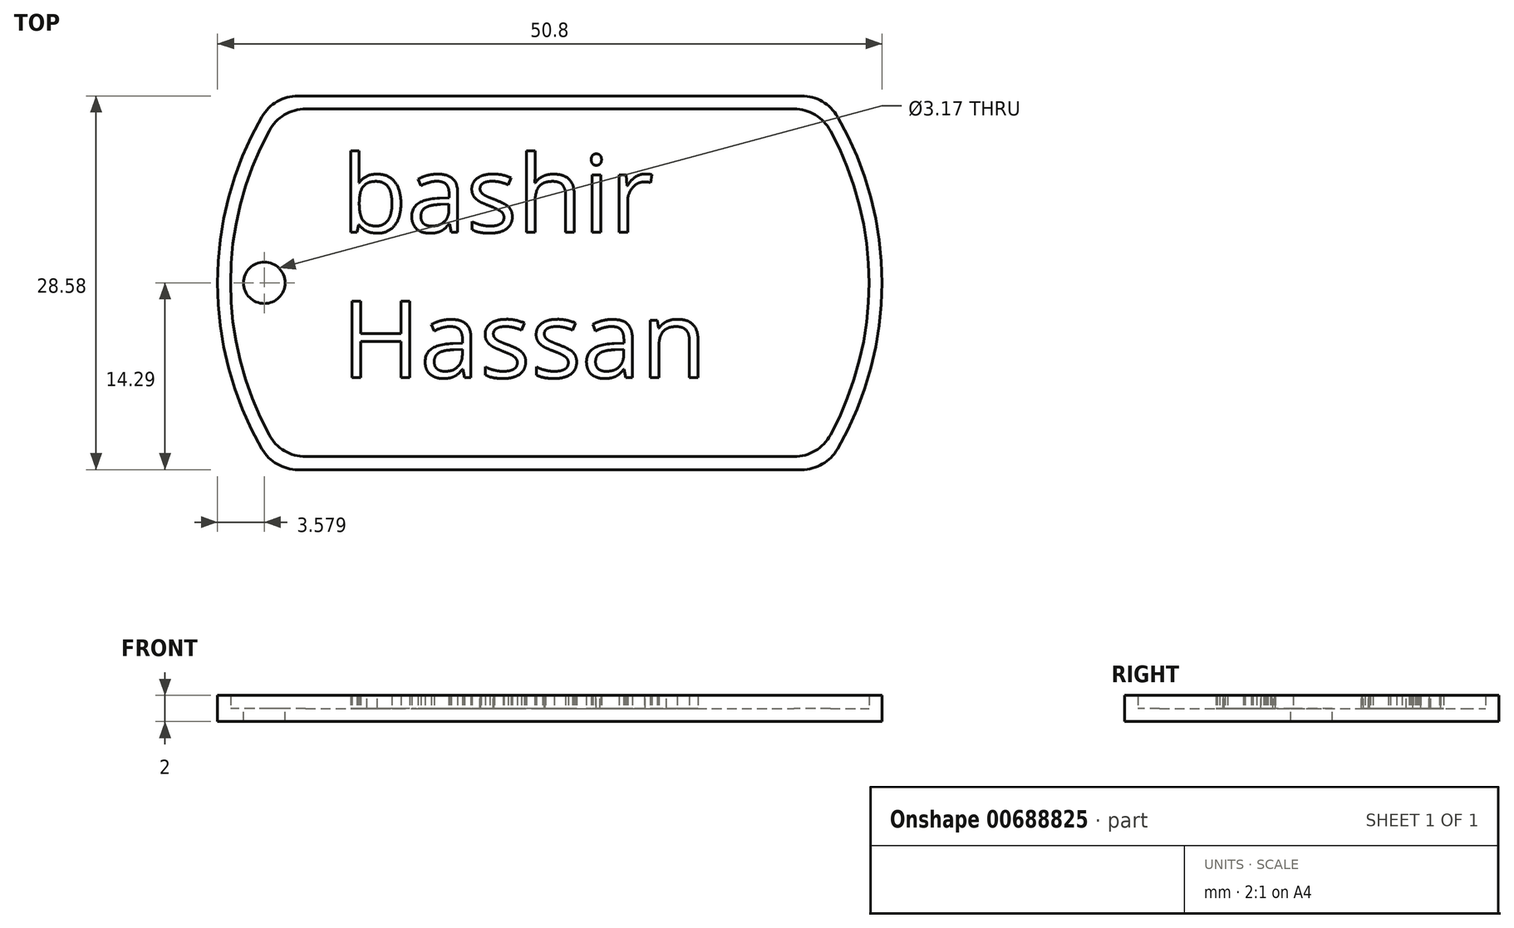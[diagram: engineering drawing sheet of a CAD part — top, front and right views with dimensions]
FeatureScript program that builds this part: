
annotation { "Feature Type Name" : "Feature", "Feature Type Description" : "" }
export const myFeature = defineFeature(function(context is Context, id is Id, definition is map)
    precondition{}
    {
        {
            var Q0;
            Q0=qCreatedBy(makeId("Top.planeOp"),FACE);
            var sketch = newSketch(context, id + "F0", { "sketchPlane" : qUnion([Q0])});
            skArc(sketch, "E0", {"start": v(-22, 12.7) * mm, "mid": v(-25.4, 0) * mm, "end": v(-22, -12.7) * mm});
            skLineSegment(sketch, "E1.top", {"start": v(-19.25, -14.29) * mm, "end": v(19.25, -14.29) * mm});
            skArc(sketch, "E2.trimOffspring", {"start": v(22, -12.7) * mm, "mid": v(25.4, 0) * mm, "end": v(22, 12.7) * mm});
            skLineSegment(sketch, "E3", {"start": v(-19.25, 14.29) * mm, "end": v(19.25, 14.29) * mm});
            skPoint(sketch, "E4.visualSharp", {"position": v(-21, 14.29) * mm});
            skArc(sketch, "E4.filletArc", {"start": v(-19.25, 14.29) * mm, "mid": v(-20.83, 13.86) * mm, "end": v(-22, 12.7) * mm});
            skPoint(sketch, "E5.visualSharp", {"position": v(21, 14.29) * mm});
            skArc(sketch, "E5.filletArc", {"start": v(22, 12.7) * mm, "mid": v(20.83, 13.86) * mm, "end": v(19.25, 14.29) * mm});
            skPoint(sketch, "E6.visualSharp", {"position": v(21, -14.29) * mm});
            skArc(sketch, "E6.filletArc", {"start": v(19.25, -14.29) * mm, "mid": v(20.83, -13.86) * mm, "end": v(22, -12.7) * mm});
            skPoint(sketch, "E7.visualSharp", {"position": v(-21, -14.29) * mm});
            skArc(sketch, "E7.filletArc", {"start": v(-22, -12.7) * mm, "mid": v(-20.83, -13.86) * mm, "end": v(-19.25, -14.29) * mm});
            skSolve(sketch);
        }
        {
            var Q0;
            Q0=makeQuery(id+"F0.imprint","IMPRINT",FACE,{"disambiguationData":[TD([[makeQuery(id+"F0.imprint","IMPRINT",EDGE,{"derivedFrom":sQuery(id+"F0.wireOp",EDGE,"E0")}),1.0]])]});
            extrude(context, id + "F1", {"entities" : qUnion([Q0]), "depth" : 1 * mm, "offsetDistance" : 25.4 * mm});
        }
        {
            var Q0;
            Q0=makeQuery(id+"F1.opExtrude","CAP_FACE",FACE,{"disambiguationData":[OSD([sQuery(id+"F0.wireOp",EDGE,"E0"),sQuery(id+"F0.wireOp",EDGE,"E1.top"),sQuery(id+"F0.wireOp",EDGE,"E2.trimOffspring"),sQuery(id+"F0.wireOp",EDGE,"E3"),sQuery(id+"F0.wireOp",EDGE,"E4.filletArc"),sQuery(id+"F0.wireOp",EDGE,"E5.filletArc"),sQuery(id+"F0.wireOp",EDGE,"E6.filletArc"),sQuery(id+"F0.wireOp",EDGE,"E7.filletArc")])],"isStart":false});
            var sketch = newSketch(context, id + "F2", { "sketchPlane" : qUnion([Q0])});
            skLineSegment(sketch, "E8.0", {"start": v(-18.66, 13.29) * mm, "end": v(18.66, 13.29) * mm});
            skArc(sketch, "E8.1", {"start": v(-21.45, 11.63) * mm, "mid": v(-24.4, 0) * mm, "end": v(-21.45, -11.63) * mm});
            skLineSegment(sketch, "E8.2", {"start": v(-18.66, -13.29) * mm, "end": v(18.66, -13.29) * mm});
            skArc(sketch, "E8.3", {"start": v(21.45, -11.63) * mm, "mid": v(24.4, 0) * mm, "end": v(21.45, 11.63) * mm});
            skPoint(sketch, "E9.visualSharp", {"position": v(-20.46, 13.29) * mm});
            skArc(sketch, "E9.filletArc", {"start": v(-18.66, 13.29) * mm, "mid": v(-20.29, 12.84) * mm, "end": v(-21.45, 11.63) * mm});
            skPoint(sketch, "E10.visualSharp", {"position": v(20.46, 13.29) * mm});
            skArc(sketch, "E10.filletArc", {"start": v(21.45, 11.63) * mm, "mid": v(20.29, 12.84) * mm, "end": v(18.66, 13.29) * mm});
            skPoint(sketch, "E11.visualSharp", {"position": v(20.46, -13.29) * mm});
            skArc(sketch, "E11.filletArc", {"start": v(18.66, -13.29) * mm, "mid": v(20.29, -12.84) * mm, "end": v(21.45, -11.63) * mm});
            skPoint(sketch, "E12.visualSharp", {"position": v(-20.46, -13.29) * mm});
            skArc(sketch, "E12.filletArc", {"start": v(-21.45, -11.63) * mm, "mid": v(-20.29, -12.84) * mm, "end": v(-18.66, -13.29) * mm});
            skLineSegment(sketch, "E13.0", {"start": v(-19.25, 14.29) * mm, "end": v(19.25, 14.29) * mm});
            skArc(sketch, "E13.1", {"start": v(-22, 12.7) * mm, "mid": v(-25.4, 0) * mm, "end": v(-22, -12.7) * mm});
            skLineSegment(sketch, "E13.2", {"start": v(-19.25, -14.29) * mm, "end": v(19.25, -14.29) * mm});
            skArc(sketch, "E13.3", {"start": v(22, -12.7) * mm, "mid": v(25.4, 0) * mm, "end": v(22, 12.7) * mm});
            skPoint(sketch, "E14.visualSharp", {"position": v(-21, -14.29) * mm});
            skArc(sketch, "E14.filletArc", {"start": v(-22, -12.7) * mm, "mid": v(-20.83, -13.86) * mm, "end": v(-19.25, -14.29) * mm});
            skPoint(sketch, "E15.visualSharp", {"position": v(21, -14.29) * mm});
            skArc(sketch, "E15.filletArc", {"start": v(19.25, -14.29) * mm, "mid": v(20.83, -13.86) * mm, "end": v(22, -12.7) * mm});
            skPoint(sketch, "E16.visualSharp", {"position": v(21, 14.29) * mm});
            skArc(sketch, "E16.filletArc", {"start": v(22, 12.7) * mm, "mid": v(20.83, 13.86) * mm, "end": v(19.25, 14.29) * mm});
            skPoint(sketch, "E17.visualSharp", {"position": v(-21, 14.29) * mm});
            skArc(sketch, "E17.filletArc", {"start": v(-19.25, 14.29) * mm, "mid": v(-20.83, 13.86) * mm, "end": v(-22, 12.7) * mm});
            skSolve(sketch);
        }
        {
            var Q0;
            Q0=makeQuery(id+"F2.imprint","IMPRINT",FACE,{"disambiguationData":[TD([[makeQuery(id+"F2.imprint","IMPRINT",EDGE,{"derivedFrom":sQuery(id+"F2.wireOp",EDGE,"E8.0")}),1.0]])]});
            extrude(context, id + "F3", {"entities" : qUnion([Q0]), "operationType" : NewBodyOperationType.ADD, "depth" : 1 * mm, "offsetDistance" : 25.4 * mm});
        }
        {
            var Q0;
            Q0=makeQuery(id+"F1.opExtrude","CAP_FACE",FACE,{"disambiguationData":[OSD([sQuery(id+"F0.wireOp",EDGE,"E0"),sQuery(id+"F0.wireOp",EDGE,"E1.top"),sQuery(id+"F0.wireOp",EDGE,"E2.trimOffspring"),sQuery(id+"F0.wireOp",EDGE,"E3"),sQuery(id+"F0.wireOp",EDGE,"E4.filletArc"),sQuery(id+"F0.wireOp",EDGE,"E5.filletArc"),sQuery(id+"F0.wireOp",EDGE,"E6.filletArc"),sQuery(id+"F0.wireOp",EDGE,"E7.filletArc")])],"isStart":false});
            var sketch = newSketch(context, id + "F4", { "sketchPlane" : qUnion([Q0])});
            skCircle(sketch, "E18", {"center": v(-21.82, 0) * mm, "radius": 1.59 * mm});
            skSolve(sketch);
        }
        {
            var Q0;
            Q0=makeQuery(id+"F4.imprint","IMPRINT",FACE,{"disambiguationData":[TD([[makeQuery(id+"F4.imprint","IMPRINT",EDGE,{"derivedFrom":sQuery(id+"F4.wireOp",EDGE,"E18")}),1.0]])]});
            extrude(context, id + "F5", {"entities" : qUnion([Q0]), "operationType" : NewBodyOperationType.REMOVE, "oppositeDirection" : true, "depth" : 1 * mm, "offsetDistance" : 25.4 * mm});
        }
        {
            var Q0;
            Q0=makeQuery(id+"F1.opExtrude","CAP_FACE",FACE,{"disambiguationData":[OSD([sQuery(id+"F0.wireOp",EDGE,"E0"),sQuery(id+"F0.wireOp",EDGE,"E1.top"),sQuery(id+"F0.wireOp",EDGE,"E2.trimOffspring"),sQuery(id+"F0.wireOp",EDGE,"E3"),sQuery(id+"F0.wireOp",EDGE,"E4.filletArc"),sQuery(id+"F0.wireOp",EDGE,"E5.filletArc"),sQuery(id+"F0.wireOp",EDGE,"E6.filletArc"),sQuery(id+"F0.wireOp",EDGE,"E7.filletArc")])],"isStart":false});
            var sketch = newSketch(context, id + "F6", { "sketchPlane" : qUnion([Q0])});
            skText(sketch, "E19", { "text": "bashir \nHassan", "fontName": "OpenSans-Regular.ttf"});
            const initialGuessF6  = {"E19": [-0.01593, 0.00387, 1, 0, 0.00588]};
            skSetInitialGuess(sketch, initialGuessF6);
            skSolve(sketch);
        }
        {
            var Q0;
            Q0 = qSketchRegion(id + "F6", true);
            extrude(context, id + "F7", {"entities" : qUnion([Q0]), "operationType" : NewBodyOperationType.ADD, "depth" : 1 * mm, "offsetDistance" : 25.4 * mm});
        }
    });
